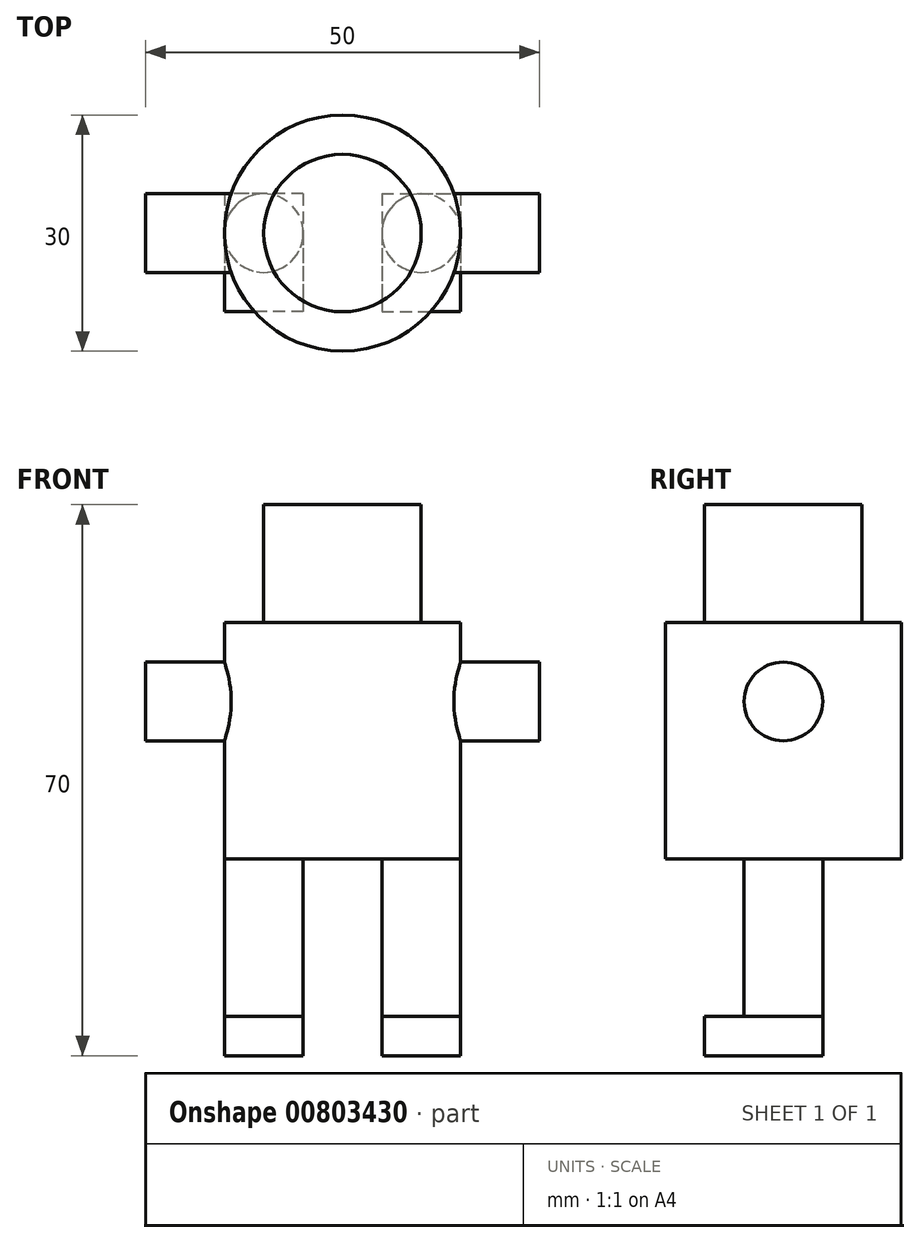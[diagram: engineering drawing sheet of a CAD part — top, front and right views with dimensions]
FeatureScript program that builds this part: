
annotation { "Feature Type Name" : "Feature", "Feature Type Description" : "" }
export const myFeature = defineFeature(function(context is Context, id is Id, definition is map)
    precondition{}
    {
        {
            var Q0;
            Q0=qCreatedBy(makeId("Top.planeOp"),FACE);
            var sketch = newSketch(context, id + "F0", { "sketchPlane" : qUnion([Q0])});
            skCircle(sketch, "E0", {"center": v(-10, 0) * mm, "radius": 5 * mm});
            skCircle(sketch, "E1", {"center": v(10, 0) * mm, "radius": 5 * mm});
            skSolve(sketch);
        }
        {
            var Q0;
            Q0=makeQuery(id+"F0.imprint","IMPRINT",FACE,{"disambiguationData":[TD([[makeQuery(id+"F0.imprint","IMPRINT",EDGE,{"derivedFrom":sQuery(id+"F0.wireOp",EDGE,"E1")}),1.0]])]});
            var Q1;
            Q1=makeQuery(id+"F0.imprint","IMPRINT",FACE,{"disambiguationData":[TD([[makeQuery(id+"F0.imprint","IMPRINT",EDGE,{"derivedFrom":sQuery(id+"F0.wireOp",EDGE,"E0")}),1.0]])]});
            extrude(context, id + "F1", {"entities" : qUnion([Q0, Q1]), "oppositeDirection" : true, "depth" : 20 * mm, "offsetDistance" : 25 * mm});
        }
        {
            var Q0;
            Q0=qCreatedBy(makeId("Top.planeOp"),FACE);
            var sketch = newSketch(context, id + "F2", { "sketchPlane" : qUnion([Q0])});
            skCircle(sketch, "E2", {"center": v(0, 0) * mm, "radius": 15 * mm});
            skSolve(sketch);
        }
        {
            var Q0;
            Q0=makeQuery(id+"F2.imprint","IMPRINT",FACE,{"disambiguationData":[TD([[makeQuery(id+"F2.imprint","IMPRINT",EDGE,{"derivedFrom":sQuery(id+"F2.wireOp",EDGE,"E2")}),1.0]])]});
            extrude(context, id + "F3", {"entities" : qUnion([Q0]), "depth" : 30 * mm, "offsetDistance" : 25 * mm});
        }
        {
            var Q0;
            Q0=qCreatedBy(makeId("Right.planeOp"),FACE);
            var sketch = newSketch(context, id + "F4", { "sketchPlane" : qUnion([Q0])});
            skCircle(sketch, "E3", {"center": v(0, 20) * mm, "radius": 5 * mm});
            skSolve(sketch);
        }
        {
            var Q0;
            Q0 = qSketchRegion(id + "F4", true);
            extrude(context, id + "F5", {"entities" : qUnion([Q0]), "operationType" : NewBodyOperationType.ADD, "depth" : 25 * mm, "offsetDistance" : 25 * mm});
        }
        {
            var Q0;
            Q0=qCreatedBy(makeId("Right.planeOp"),FACE);
            var sketch = newSketch(context, id + "F6", { "sketchPlane" : qUnion([Q0])});
            skCircle(sketch, "E4", {"center": v(0, 20) * mm, "radius": 5 * mm});
            skSolve(sketch);
        }
        {
            var Q0;
            Q0 = qSketchRegion(id + "F6", true);
            extrude(context, id + "F7", {"entities" : qUnion([Q0]), "operationType" : NewBodyOperationType.ADD, "oppositeDirection" : true, "depth" : 25 * mm, "offsetDistance" : 25 * mm});
        }
        {
            var Q0;
            Q0=makeQuery(id+"F3.opExtrude","CAP_FACE",FACE,{"disambiguationData":[OSD([sQuery(id+"F2.wireOp",EDGE,"E2")])],"isStart":false});
            var sketch = newSketch(context, id + "F8", { "sketchPlane" : qUnion([Q0])});
            skCircle(sketch, "E5", {"center": v(0, 0) * mm, "radius": 10 * mm});
            skSolve(sketch);
        }
        {
            var Q0;
            Q0 = qSketchRegion(id + "F8", true);
            extrude(context, id + "F9", {"entities" : qUnion([Q0]), "operationType" : NewBodyOperationType.ADD, "depth" : 15 * mm, "offsetDistance" : 25 * mm});
        }
        {
            var Q0;
            Q0=makeQuery(id+"F1.opExtrude","CAP_FACE",FACE,{"disambiguationData":[OSD([sQuery(id+"F0.wireOp",EDGE,"E0")])],"isStart":false});
            var sketch = newSketch(context, id + "F10", { "sketchPlane" : qUnion([Q0])});
            skLineSegment(sketch, "E6.bottom", {"start": v(-5, -5) * mm, "end": v(-15, -5) * mm});
            skLineSegment(sketch, "E6.top", {"start": v(-5, 10) * mm, "end": v(-15, 10) * mm});
            skLineSegment(sketch, "E6.left", {"start": v(-5, -5) * mm, "end": v(-5, 10) * mm});
            skLineSegment(sketch, "E6.right", {"start": v(-15, -5) * mm, "end": v(-15, 10) * mm});
            skPoint(sketch, "E7", {"position": v(-10, -5) * mm});
            skPoint(sketch, "E8", {"position": v(-15, 0) * mm});
            skSolve(sketch);
        }
        {
            var Q0;
            Q0 = qSketchRegion(id + "F10", true);
            extrude(context, id + "F11", {"entities" : qUnion([Q0]), "operationType" : NewBodyOperationType.ADD, "depth" : 5 * mm, "offsetDistance" : 25 * mm});
        }
        {
            var Q0;
            Q0=makeQuery(id+"F1.opExtrude","CAP_FACE",FACE,{"disambiguationData":[OSD([sQuery(id+"F0.wireOp",EDGE,"E1")])],"isStart":false});
            var sketch = newSketch(context, id + "F12", { "sketchPlane" : qUnion([Q0])});
            skLineSegment(sketch, "E9.bottom", {"start": v(5, -5) * mm, "end": v(15, -5) * mm});
            skLineSegment(sketch, "E9.top", {"start": v(5, 10) * mm, "end": v(15, 10) * mm});
            skLineSegment(sketch, "E9.left", {"start": v(5, -5) * mm, "end": v(5, 10) * mm});
            skLineSegment(sketch, "E9.right", {"start": v(15, -5) * mm, "end": v(15, 10) * mm});
            skPoint(sketch, "E10", {"position": v(5, 0) * mm});
            skPoint(sketch, "E11", {"position": v(10, -5) * mm});
            skPoint(sketch, "E12", {"position": v(10, 0) * mm});
            skSolve(sketch);
        }
        {
            var Q0;
            Q0 = qSketchRegion(id + "F12", true);
            extrude(context, id + "F13", {"entities" : qUnion([Q0]), "operationType" : NewBodyOperationType.ADD, "depth" : 5 * mm, "offsetDistance" : 25 * mm});
        }
    });
